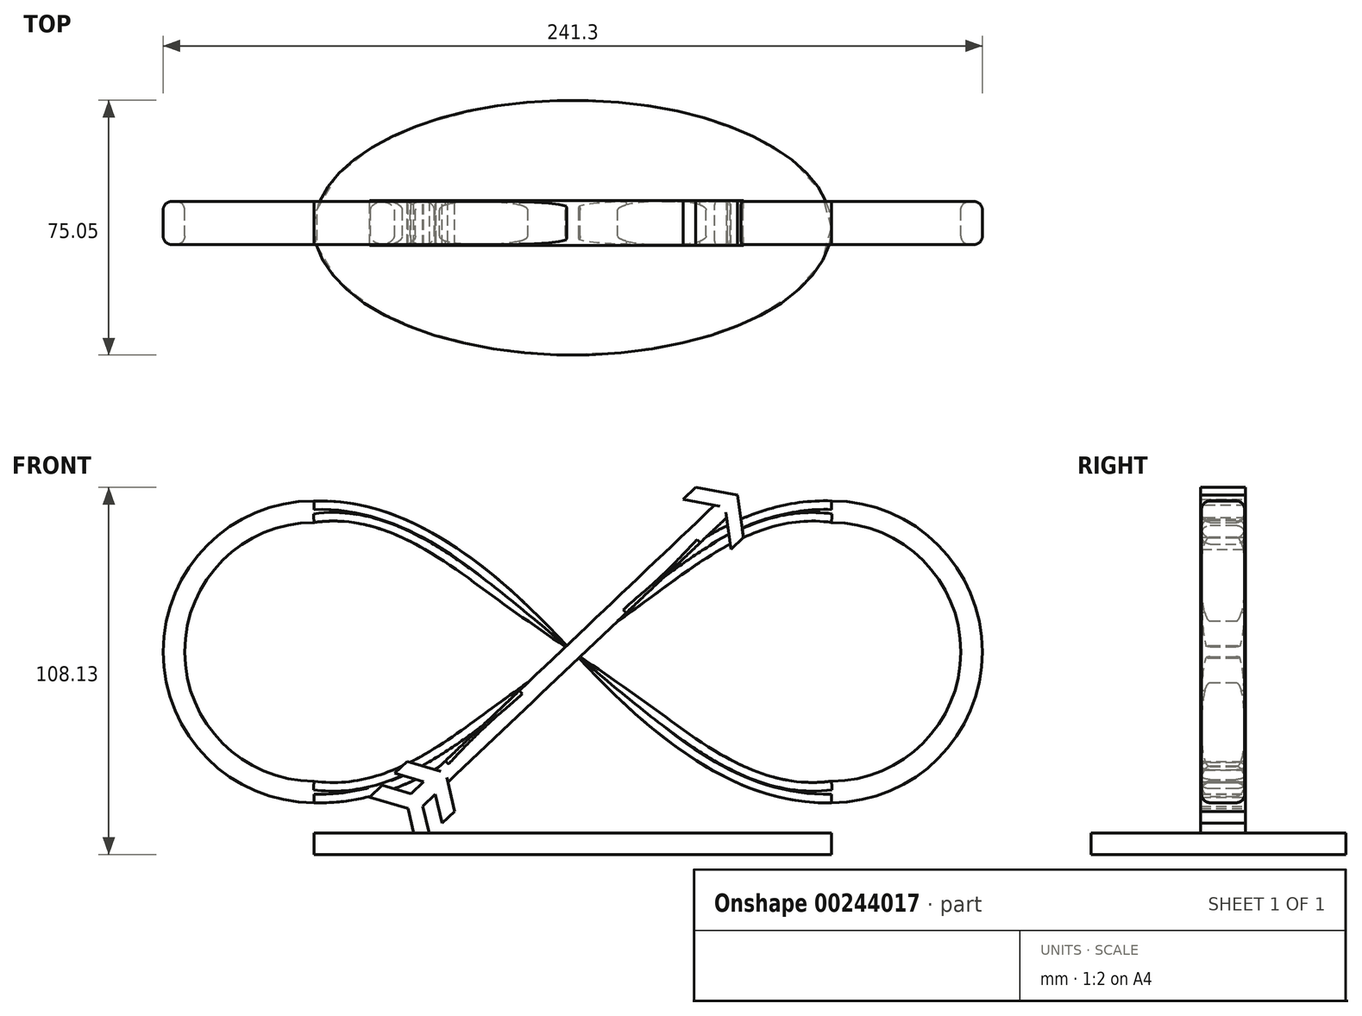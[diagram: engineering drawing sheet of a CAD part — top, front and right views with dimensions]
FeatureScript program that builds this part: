
annotation { "Feature Type Name" : "Feature", "Feature Type Description" : "" }
export const myFeature = defineFeature(function(context is Context, id is Id, definition is map)
    precondition{}
    {
        {
            var Q0;
            Q0=qCreatedBy(makeId("Front.planeOp"),FACE);
            var sketch = newSketch(context, id + "F0", { "sketchPlane" : qUnion([Q0])});
            skCircle(sketch, "E0", {"center": v(-76.2, 0) * mm, "radius": 38.1 * mm});
            skCircle(sketch, "E1", {"center": v(76.2, 0) * mm, "radius": 38.1 * mm});
            skFitSpline(sketch, "E2", {"points": [v(-76.2, 38.1) * mm, v(-25.4, 17.78) * mm, v(0, 0) * mm, v(25.4, -17.78) * mm, v(76.2, -38.1) * mm], "startDerivative": vector(211.41, 31.16) * mm, "endDerivative": vector(213.7, 30.04) * mm});
            skFitSpline(sketch, "E3", {"points": [v(76.2, 38.1) * mm, v(25.4, 17.78) * mm, v(0, 0) * mm, v(-25.4, -17.78) * mm, v(-76.2, -38.1) * mm], "startDerivative": vector(-211.41, 31.16) * mm, "endDerivative": vector(-211.41, 31.16) * mm});
            skCircle(sketch, "E4", {"center": v(-76.2, 0) * mm, "radius": 44.45 * mm});
            skCircle(sketch, "E5", {"center": v(76.2, 0) * mm, "radius": 44.45 * mm});
            skFitSpline(sketch, "E6", {"points": [v(-76.2, -44.45) * mm, v(-25.4, -24.13) * mm, v(0, 0) * mm, v(25.4, 24.13) * mm, v(76.2, 44.45) * mm], "startDerivative": vector(219.34, -7.84) * mm, "endDerivative": vector(219.34, -7.84) * mm});
            skFitSpline(sketch, "E7", {"points": [v(-76.2, 44.45) * mm, v(-25.4, 24.13) * mm, v(0, 0) * mm, v(25.4, -24.13) * mm, v(76.2, -44.45) * mm], "startDerivative": vector(219.34, 7.84) * mm, "endDerivative": vector(219.34, 7.84) * mm});
            skLineSegment(sketch, "E8", {"start": v(-48.54, -46.12) * mm, "end": v(48.54, 46.12) * mm});
            skLineSegment(sketch, "E9", {"start": v(-50.3, -44.27) * mm, "end": v(-48.54, -46.12) * mm});
            skLineSegment(sketch, "E10", {"start": v(-48.54, -46.12) * mm, "end": v(-46.8, -47.96) * mm});
            skLineSegment(sketch, "E11", {"start": v(-46.8, -47.96) * mm, "end": v(45.28, 39.51) * mm});
            skLineSegment(sketch, "E12", {"start": v(-48.54, -46.12) * mm, "end": v(-59.8, -42.79) * mm});
            skLineSegment(sketch, "E13", {"start": v(-59.8, -42.79) * mm, "end": v(-56.11, -39.3) * mm});
            skLineSegment(sketch, "E14", {"start": v(-56.11, -39.3) * mm, "end": v(-44.86, -42.62) * mm});
            skLineSegment(sketch, "E15", {"start": v(-44.86, -42.62) * mm, "end": v(-42.11, -54.02) * mm});
            skLineSegment(sketch, "E16", {"start": v(-42.11, -54.02) * mm, "end": v(-45.8, -57.52) * mm});
            skLineSegment(sketch, "E17", {"start": v(-45.8, -57.52) * mm, "end": v(-48.54, -46.12) * mm});
            skLineSegment(sketch, "E18", {"start": v(-41.18, -39.12) * mm, "end": v(-38.43, -50.52) * mm});
            skLineSegment(sketch, "E19", {"start": v(-38.43, -50.52) * mm, "end": v(-34.75, -47.03) * mm});
            skLineSegment(sketch, "E20", {"start": v(-34.75, -47.03) * mm, "end": v(-37.5, -35.62) * mm});
            skLineSegment(sketch, "E21", {"start": v(-37.5, -35.62) * mm, "end": v(-48.74, -32.3) * mm});
            skLineSegment(sketch, "E22", {"start": v(-48.74, -32.3) * mm, "end": v(-52.43, -35.8) * mm});
            skLineSegment(sketch, "E23", {"start": v(-52.43, -35.8) * mm, "end": v(-41.18, -39.12) * mm});
            skLineSegment(sketch, "E24", {"start": v(41.78, 43.2) * mm, "end": v(-50.3, -44.27) * mm});
            skLineSegment(sketch, "E25", {"start": v(41.78, 43.2) * mm, "end": v(32.55, 44.94) * mm});
            skLineSegment(sketch, "E26", {"start": v(32.55, 44.94) * mm, "end": v(36.23, 48.44) * mm});
            skLineSegment(sketch, "E27", {"start": v(36.23, 48.44) * mm, "end": v(48.54, 46.12) * mm});
            skLineSegment(sketch, "E28", {"start": v(45.28, 39.51) * mm, "end": v(46.55, 30.2) * mm});
            skLineSegment(sketch, "E29", {"start": v(46.55, 30.2) * mm, "end": v(50.23, 33.7) * mm});
            skLineSegment(sketch, "E30", {"start": v(50.23, 33.7) * mm, "end": v(48.54, 46.12) * mm});
            skSolve(sketch);
        }
        {
            var Q0;
            {var subQ0=sQuery(id+"F0.wireOp",EDGE,"E4");var subQ3=sQuery(id+"F0.wireOp",EDGE,"E7");var subQ5=makeQuery(id+"F0.imprint","INTERSECT",VERTEX,{"derivedFrom":[subQ0,subQ3]});Q0=makeQuery(id+"F0.imprint","IMPRINT",FACE,{"disambiguationData":[TD([[makeQuery(id+"F0.imprint","IMPRINT",EDGE,{"disambiguationData":[TD([[subQ5,1.0]])],"derivedFrom":subQ0}),-1.0]])]});}
            var Q1;
            {var subQ0=sQuery(id+"F0.wireOp",EDGE,"E4");var subQ3=sQuery(id+"F0.wireOp",EDGE,"E6");var subQ5=makeQuery(id+"F0.imprint","INTERSECT",VERTEX,{"derivedFrom":[subQ0,subQ3]});Q1=makeQuery(id+"F0.imprint","IMPRINT",FACE,{"disambiguationData":[TD([[makeQuery(id+"F0.imprint","IMPRINT",EDGE,{"disambiguationData":[TD([[subQ5,-1.0]])],"derivedFrom":subQ0}),-1.0]])]});}
            var Q2;
            {var subQ0=sQuery(id+"F0.wireOp",EDGE,"E5");var subQ3=sQuery(id+"F0.wireOp",EDGE,"E6");var subQ5=makeQuery(id+"F0.imprint","INTERSECT",VERTEX,{"derivedFrom":[subQ0,subQ3]});Q2=makeQuery(id+"F0.imprint","IMPRINT",FACE,{"disambiguationData":[TD([[makeQuery(id+"F0.imprint","IMPRINT",EDGE,{"disambiguationData":[TD([[subQ5,-1.0]])],"derivedFrom":subQ0}),-1.0]])]});}
            var Q3;
            {var subQ1=sQuery(id+"F0.wireOp",EDGE,"E1");var subQ5=sQuery(id+"F0.wireOp",EDGE,"E2");var subQ6=makeQuery(id+"F0.imprint","INTERSECT",VERTEX,{"derivedFrom":[subQ1,subQ5]});Q3=makeQuery(id+"F0.imprint","IMPRINT",FACE,{"disambiguationData":[TD([[makeQuery(id+"F0.imprint","IMPRINT",EDGE,{"disambiguationData":[TD([[subQ6,-1.0]])],"derivedFrom":subQ1}),-1.0]])]});}
            var Q4;
            {var subQ0=sQuery(id+"F0.wireOp",EDGE,"E13");var subQ1=sQuery(id+"F0.wireOp",EDGE,"E4");var subQ2=makeQuery(id+"F0.imprint","INTERSECT",VERTEX,{"derivedFrom":[subQ1,subQ0]});Q4=makeQuery(id+"F0.imprint","IMPRINT",FACE,{"disambiguationData":[TD([[makeQuery(id+"F0.imprint","IMPRINT",EDGE,{"disambiguationData":[TD([[subQ2,-1.0]])],"derivedFrom":subQ1}),-1.0]])]});}
            var Q5;
            {var subQ0=sQuery(id+"F0.wireOp",EDGE,"E13");var subQ1=sQuery(id+"F0.wireOp",EDGE,"E4");var subQ2=makeQuery(id+"F0.imprint","INTERSECT",VERTEX,{"derivedFrom":[subQ1,subQ0]});Q5=makeQuery(id+"F0.imprint","IMPRINT",FACE,{"disambiguationData":[TD([[makeQuery(id+"F0.imprint","IMPRINT",EDGE,{"disambiguationData":[TD([[subQ2,-1.0]])],"derivedFrom":subQ1}),1.0]])]});}
            var Q6;
            {var subQ14=sQuery(id+"F0.wireOp",EDGE,"E2");var subQ15=sQuery(id+"F0.wireOp",EDGE,"E0");var subQ16=makeQuery(id+"F0.imprint","INTERSECT",VERTEX,{"derivedFrom":[subQ15,subQ14]});Q6=makeQuery(id+"F0.imprint","IMPRINT",FACE,{"disambiguationData":[TD([[makeQuery(id+"F0.imprint","IMPRINT",EDGE,{"disambiguationData":[TD([[subQ16,-1.0]])],"derivedFrom":subQ15}),-1.0]])]});}
            var Q7;
            {var subQ3=sQuery(id+"F0.wireOp",EDGE,"E3");var subQ5=sQuery(id+"F0.wireOp",EDGE,"E21");var subQ6=makeQuery(id+"F0.imprint","INTERSECT",VERTEX,{"derivedFrom":[subQ3,subQ5]});Q7=makeQuery(id+"F0.imprint","IMPRINT",FACE,{"disambiguationData":[TD([[makeQuery(id+"F0.imprint","IMPRINT",EDGE,{"disambiguationData":[TD([[subQ6,-1.0]])],"derivedFrom":subQ3}),1.0]])]});}
            var Q8;
            {var subQ0=sQuery(id+"F0.wireOp",EDGE,"E14");var subQ1=sQuery(id+"F0.wireOp",EDGE,"E4");var subQ2=makeQuery(id+"F0.imprint","INTERSECT",VERTEX,{"derivedFrom":[subQ1,subQ0]});Q8=makeQuery(id+"F0.imprint","IMPRINT",FACE,{"disambiguationData":[TD([[makeQuery(id+"F0.imprint","IMPRINT",EDGE,{"disambiguationData":[TD([[subQ2,-1.0]])],"derivedFrom":subQ1}),-1.0]])]});}
            var Q9;
            {var subQ0=sQuery(id+"F0.wireOp",EDGE,"E23");var subQ1=sQuery(id+"F0.wireOp",EDGE,"E4");var subQ2=makeQuery(id+"F0.imprint","INTERSECT",VERTEX,{"derivedFrom":[subQ1,subQ0]});Q9=makeQuery(id+"F0.imprint","IMPRINT",FACE,{"disambiguationData":[TD([[makeQuery(id+"F0.imprint","IMPRINT",EDGE,{"disambiguationData":[TD([[subQ2,-1.0]])],"derivedFrom":subQ1}),-1.0]])]});}
            var Q10;
            {var subQ0=sQuery(id+"F0.wireOp",EDGE,"E4");var subQ1=sQuery(id+"F0.wireOp",EDGE,"E3");var subQ2=makeQuery(id+"F0.imprint","INTERSECT",VERTEX,{"derivedFrom":[subQ1,subQ0]});Q10=makeQuery(id+"F0.imprint","IMPRINT",FACE,{"disambiguationData":[TD([[makeQuery(id+"F0.imprint","IMPRINT",EDGE,{"disambiguationData":[TD([[subQ2,-1.0]])],"derivedFrom":subQ1}),1.0]])]});}
            var Q11;
            {var subQ1=sQuery(id+"F0.wireOp",EDGE,"E3");var subQ7=sQuery(id+"F0.wireOp",EDGE,"E24");var subQ9=makeQuery(id+"F0.imprint","INTERSECT",VERTEX,{"derivedFrom":[subQ1,subQ7]});Q11=makeQuery(id+"F0.imprint","IMPRINT",FACE,{"disambiguationData":[TD([[makeQuery(id+"F0.imprint","IMPRINT",EDGE,{"disambiguationData":[TD([[subQ9,-1.0]])],"derivedFrom":subQ1}),1.0]])]});}
            var Q12;
            {var subQ0=sQuery(id+"F0.wireOp",EDGE,"E24");var subQ4=sQuery(id+"F0.wireOp",EDGE,"E6");var subQ6=makeQuery(id+"F0.imprint","INTERSECT",VERTEX,{"derivedFrom":[subQ4,subQ0]});Q12=makeQuery(id+"F0.imprint","IMPRINT",FACE,{"disambiguationData":[TD([[makeQuery(id+"F0.imprint","IMPRINT",EDGE,{"disambiguationData":[TD([[subQ6,-1.0]])],"derivedFrom":subQ4}),1.0]])]});}
            var Q13;
            {var subQ0=sQuery(id+"F0.wireOp",EDGE,"E24");var subQ1=sQuery(id+"F0.wireOp",EDGE,"E2");var subQ2=makeQuery(id+"F0.imprint","INTERSECT",VERTEX,{"derivedFrom":[subQ1,subQ0]});Q13=makeQuery(id+"F0.imprint","IMPRINT",FACE,{"disambiguationData":[TD([[makeQuery(id+"F0.imprint","IMPRINT",EDGE,{"disambiguationData":[TD([[subQ2,-1.0]])],"derivedFrom":subQ0}),1.0]])]});}
            var Q14;
            {var subQ0=sQuery(id+"F0.wireOp",EDGE,"E11");var subQ3=sQuery(id+"F0.wireOp",EDGE,"E7");var subQ5=makeQuery(id+"F0.imprint","INTERSECT",VERTEX,{"derivedFrom":[subQ3,subQ0]});Q14=makeQuery(id+"F0.imprint","IMPRINT",FACE,{"disambiguationData":[TD([[makeQuery(id+"F0.imprint","IMPRINT",EDGE,{"disambiguationData":[TD([[subQ5,-1.0]])],"derivedFrom":subQ0}),1.0]])]});}
            var Q15;
            {var subQ0=sQuery(id+"F0.wireOp",EDGE,"E24");var subQ3=sQuery(id+"F0.wireOp",EDGE,"E7");var subQ5=makeQuery(id+"F0.imprint","INTERSECT",VERTEX,{"derivedFrom":[subQ3,subQ0]});Q15=makeQuery(id+"F0.imprint","IMPRINT",FACE,{"disambiguationData":[TD([[makeQuery(id+"F0.imprint","IMPRINT",EDGE,{"disambiguationData":[TD([[subQ5,-1.0]])],"derivedFrom":subQ0}),1.0]])]});}
            var Q16;
            {var subQ0=sQuery(id+"F0.wireOp",EDGE,"E8");var subQ1=sQuery(id+"F0.wireOp",EDGE,"E6");var subQ2=makeQuery(id+"F0.imprint","INTERSECT",VERTEX,{"disambiguationData":[OD(0.0)],"derivedFrom":[subQ1,subQ0]});Q16=makeQuery(id+"F0.imprint","IMPRINT",FACE,{"disambiguationData":[TD([[makeQuery(id+"F0.imprint","IMPRINT",EDGE,{"disambiguationData":[TD([[subQ2,-1.0]])],"derivedFrom":subQ1}),1.0]])]});}
            var Q17;
            {var subQ3=sQuery(id+"F0.wireOp",EDGE,"E8");var subQ4=sQuery(id+"F0.wireOp",EDGE,"E6");var subQ6=makeQuery(id+"F0.imprint","INTERSECT",VERTEX,{"disambiguationData":[OD(1.0)],"derivedFrom":[subQ4,subQ3]});Q17=makeQuery(id+"F0.imprint","IMPRINT",FACE,{"disambiguationData":[TD([[makeQuery(id+"F0.imprint","IMPRINT",EDGE,{"disambiguationData":[TD([[subQ6,-1.0]])],"derivedFrom":subQ4}),-1.0]])]});}
            var Q18;
            {var subQ0=sQuery(id+"F0.wireOp",EDGE,"E30");var subQ1=sQuery(id+"F0.wireOp",EDGE,"E5");var subQ2=makeQuery(id+"F0.imprint","INTERSECT",VERTEX,{"derivedFrom":[subQ1,subQ0]});Q18=makeQuery(id+"F0.imprint","IMPRINT",FACE,{"disambiguationData":[TD([[makeQuery(id+"F0.imprint","IMPRINT",EDGE,{"disambiguationData":[TD([[subQ2,-1.0]])],"derivedFrom":subQ1}),-1.0]])]});}
            var Q19;
            {var subQ1=sQuery(id+"F0.wireOp",EDGE,"E3");var subQ7=sQuery(id+"F0.wireOp",EDGE,"E29");var subQ9=makeQuery(id+"F0.imprint","INTERSECT",VERTEX,{"derivedFrom":[subQ1,subQ7]});Q19=makeQuery(id+"F0.imprint","IMPRINT",FACE,{"disambiguationData":[TD([[makeQuery(id+"F0.imprint","IMPRINT",EDGE,{"disambiguationData":[TD([[subQ9,-1.0]])],"derivedFrom":subQ1}),-1.0]])]});}
            var Q20;
            {var subQ1=sQuery(id+"F0.wireOp",EDGE,"E3");var subQ7=sQuery(id+"F0.wireOp",EDGE,"E5");var subQ8=makeQuery(id+"F0.imprint","INTERSECT",VERTEX,{"derivedFrom":[subQ1,subQ7]});Q20=makeQuery(id+"F0.imprint","IMPRINT",FACE,{"disambiguationData":[TD([[makeQuery(id+"F0.imprint","IMPRINT",EDGE,{"disambiguationData":[TD([[subQ8,-1.0]])],"derivedFrom":subQ1}),-1.0]])]});}
            var Q21;
            {var subQ0=sQuery(id+"F0.wireOp",EDGE,"E11");var subQ1=sQuery(id+"F0.wireOp",EDGE,"E2");var subQ2=makeQuery(id+"F0.imprint","INTERSECT",VERTEX,{"derivedFrom":[subQ1,subQ0]});Q21=makeQuery(id+"F0.imprint","IMPRINT",FACE,{"disambiguationData":[TD([[makeQuery(id+"F0.imprint","IMPRINT",EDGE,{"disambiguationData":[TD([[subQ2,-1.0]])],"derivedFrom":subQ1}),-1.0]])]});}
            var Q22;
            {var subQ0=sQuery(id+"F0.wireOp",EDGE,"E28");var subQ1=sQuery(id+"F0.wireOp",EDGE,"E3");var subQ2=makeQuery(id+"F0.imprint","INTERSECT",VERTEX,{"derivedFrom":[subQ1,subQ0]});Q22=makeQuery(id+"F0.imprint","IMPRINT",FACE,{"disambiguationData":[TD([[makeQuery(id+"F0.imprint","IMPRINT",EDGE,{"disambiguationData":[TD([[subQ2,-1.0]])],"derivedFrom":subQ1}),-1.0]])]});}
            var Q23;
            {var subQ0=sQuery(id+"F0.wireOp",EDGE,"E8");var subQ1=sQuery(id+"F0.wireOp",EDGE,"E6");var subQ2=makeQuery(id+"F0.imprint","INTERSECT",VERTEX,{"disambiguationData":[OD(1.0)],"derivedFrom":[subQ1,subQ0]});Q23=makeQuery(id+"F0.imprint","IMPRINT",FACE,{"disambiguationData":[TD([[makeQuery(id+"F0.imprint","IMPRINT",EDGE,{"disambiguationData":[TD([[subQ2,1.0]])],"derivedFrom":subQ1}),-1.0]])]});}
            var Q24;
            {var subQ0=sQuery(id+"F0.wireOp",EDGE,"E11");var subQ1=sQuery(id+"F0.wireOp",EDGE,"E2");var subQ2=makeQuery(id+"F0.imprint","INTERSECT",VERTEX,{"derivedFrom":[subQ1,subQ0]});Q24=makeQuery(id+"F0.imprint","IMPRINT",FACE,{"disambiguationData":[TD([[makeQuery(id+"F0.imprint","IMPRINT",EDGE,{"disambiguationData":[TD([[subQ2,-1.0]])],"derivedFrom":subQ0}),1.0]])]});}
            extrude(context, id + "F1", {"entities" : qUnion([Q0, Q1, Q2, Q3, Q4, Q5, Q6, Q7, Q8, Q9, Q10, Q11, Q12, Q13, Q14, Q15, Q16, Q17, Q18, Q19, Q20, Q21, Q22, Q23, Q24]), "depth" : 6.35 * mm, "hasSecondDirection" : true, "secondDirectionOppositeDirection" : true, "secondDirectionDepth" : 6.35 * mm});
        }
        {
            var Q0;
            {var subQ0=sQuery(id+"F0.wireOp",EDGE,"E2");var subQ1=makeQuery(id+"F0.imprint","INTERSECT",VERTEX,{"derivedFrom":[subQ0,sQuery(id+"F0.wireOp",EDGE,"E4")]});Q0=makeQuery(id+"F1.opExtrude","CAP_EDGE",EDGE,{"disambiguationData":[OSD([subQ0]),TDD([makeQuery(id+"F0.imprint","IMPRINT",EDGE,{"disambiguationData":[TD([[makeQuery(id+"F0.imprint","INTERSECT",VERTEX,{"derivedFrom":[sQuery(id+"F0.wireOp",EDGE,"E0"),subQ0]}),-1.0]])],"derivedFrom":subQ0}),makeQuery(id+"F0.imprint","IMPRINT",EDGE,{"disambiguationData":[TD([[subQ1,-1.0]])],"derivedFrom":subQ0})])],"isStart":true});}
            var Q1;
            {var subQ0=sQuery(id+"F0.wireOp",EDGE,"E7");var subQ1=makeQuery(id+"F0.imprint","INTERSECT",VERTEX,{"derivedFrom":[subQ0,sQuery(id+"F0.wireOp",EDGE,"E24")]});Q1=makeQuery(id+"F1.opExtrude","CAP_EDGE",EDGE,{"disambiguationData":[OSD([subQ0]),TDD([makeQuery(id+"F0.imprint","IMPRINT",EDGE,{"disambiguationData":[TD([[makeQuery(id+"F0.imprint","INTERSECT",VERTEX,{"derivedFrom":[sQuery(id+"F0.wireOp",EDGE,"E4"),subQ0]}),-1.0]])],"derivedFrom":subQ0}),makeQuery(id+"F0.imprint","IMPRINT",EDGE,{"disambiguationData":[TD([[subQ1,-1.0]])],"derivedFrom":subQ0})])],"isStart":true});}
            var Q2;
            Q2=makeQuery(id+"F1.opExtrude","CAP_EDGE",EDGE,{"disambiguationData":[OSD([sQuery(id+"F0.wireOp",EDGE,"E24")])],"isStart":true});
            var Q3;
            {var subQ0=sQuery(id+"F0.wireOp",EDGE,"E8");var subQ1=sQuery(id+"F0.wireOp",EDGE,"E6");var subQ2=makeQuery(id+"F0.imprint","INTERSECT",VERTEX,{"disambiguationData":[OD(0.0)],"derivedFrom":[subQ1,subQ0]});var subQ3=makeQuery(id+"F0.imprint","INTERSECT",VERTEX,{"derivedFrom":[subQ1,sQuery(id+"F0.wireOp",EDGE,"E24")]});var subQ4=makeQuery(id+"F0.imprint","INTERSECT",VERTEX,{"derivedFrom":[subQ1,sQuery(id+"F0.wireOp",EDGE,"E21")]});var subQ5=makeQuery(id+"F0.imprint","INTERSECT",VERTEX,{"derivedFrom":[subQ1,sQuery(id+"F0.wireOp",EDGE,"E23")]});var subQ6=makeQuery(id+"F0.imprint","INTERSECT",VERTEX,{"derivedFrom":[subQ1,sQuery(id+"F0.wireOp",EDGE,"E14")]});var subQ7=makeQuery(id+"F0.imprint","INTERSECT",VERTEX,{"derivedFrom":[subQ1,sQuery(id+"F0.wireOp",EDGE,"E13")]});Q3=makeQuery(id+"F1.opExtrude","CAP_EDGE",EDGE,{"disambiguationData":[OSD([subQ1]),TDD([makeQuery(id+"F0.imprint","IMPRINT",EDGE,{"disambiguationData":[TD([[makeQuery(id+"F0.imprint","INTERSECT",VERTEX,{"derivedFrom":[sQuery(id+"F0.wireOp",EDGE,"E4"),subQ1]}),-1.0]])],"derivedFrom":subQ1}),makeQuery(id+"F0.imprint","IMPRINT",EDGE,{"disambiguationData":[TD([[subQ7,-1.0]])],"derivedFrom":subQ1}),makeQuery(id+"F0.imprint","IMPRINT",EDGE,{"disambiguationData":[TD([[subQ6,-1.0]])],"derivedFrom":subQ1}),makeQuery(id+"F0.imprint","IMPRINT",EDGE,{"disambiguationData":[TD([[subQ5,-1.0]])],"derivedFrom":subQ1}),makeQuery(id+"F0.imprint","IMPRINT",EDGE,{"disambiguationData":[TD([[subQ4,-1.0]])],"derivedFrom":subQ1}),makeQuery(id+"F0.imprint","IMPRINT",EDGE,{"disambiguationData":[TD([[subQ3,-1.0]])],"derivedFrom":subQ1}),makeQuery(id+"F0.imprint","IMPRINT",EDGE,{"disambiguationData":[TD([[subQ2,-1.0]])],"derivedFrom":subQ1})])],"isStart":true});}
            var Q4;
            {var subQ0=sQuery(id+"F0.wireOp",EDGE,"E6");var subQ1=makeQuery(id+"F0.imprint","INTERSECT",VERTEX,{"derivedFrom":[subQ0,sQuery(id+"F0.wireOp",EDGE,"E30")]});var subQ3=makeQuery(id+"F0.imprint","INTERSECT",VERTEX,{"derivedFrom":[subQ0,sQuery(id+"F0.wireOp",EDGE,"E11")]});var subQ4=sQuery(id+"F0.wireOp",EDGE,"E8");var subQ5=makeQuery(id+"F0.imprint","INTERSECT",VERTEX,{"disambiguationData":[OD(1.0)],"derivedFrom":[subQ0,subQ4]});Q4=makeQuery(id+"F1.opExtrude","CAP_EDGE",EDGE,{"disambiguationData":[OSD([subQ0]),TDD([makeQuery(id+"F0.imprint","IMPRINT",EDGE,{"disambiguationData":[TD([[subQ5,1.0]])],"derivedFrom":subQ0}),makeQuery(id+"F0.imprint","IMPRINT",EDGE,{"disambiguationData":[TD([[subQ5,-1.0]])],"derivedFrom":subQ0}),makeQuery(id+"F0.imprint","IMPRINT",EDGE,{"disambiguationData":[TD([[subQ3,-1.0]])],"derivedFrom":subQ0}),makeQuery(id+"F0.imprint","IMPRINT",EDGE,{"disambiguationData":[TD([[subQ1,1.0]])],"derivedFrom":subQ0}),makeQuery(id+"F0.imprint","IMPRINT",EDGE,{"disambiguationData":[TD([[makeQuery(id+"F0.imprint","INTERSECT",VERTEX,{"derivedFrom":[sQuery(id+"F0.wireOp",EDGE,"E5"),subQ0]}),1.0]])],"derivedFrom":subQ0})])],"isStart":true});}
            var Q5;
            {var subQ0=sQuery(id+"F0.wireOp",EDGE,"E2");Q5=makeQuery(id+"F1.opExtrude","CAP_EDGE",EDGE,{"disambiguationData":[OSD([subQ0]),TDD([makeQuery(id+"F0.imprint","IMPRINT",EDGE,{"disambiguationData":[TD([[makeQuery(id+"F0.imprint","INTERSECT",VERTEX,{"derivedFrom":[subQ0,sQuery(id+"F0.wireOp",EDGE,"E11")]}),-1.0]])],"derivedFrom":subQ0}),makeQuery(id+"F0.imprint","IMPRINT",EDGE,{"disambiguationData":[TD([[makeQuery(id+"F0.imprint","INTERSECT",VERTEX,{"derivedFrom":[sQuery(id+"F0.wireOp",EDGE,"E1"),subQ0]}),1.0]])],"derivedFrom":subQ0})])],"isStart":true});}
            var Q6;
            {var subQ0=sQuery(id+"F0.wireOp",EDGE,"E7");var subQ1=makeQuery(id+"F0.imprint","INTERSECT",VERTEX,{"derivedFrom":[subQ0,sQuery(id+"F0.wireOp",EDGE,"E11")]});Q6=makeQuery(id+"F1.opExtrude","CAP_EDGE",EDGE,{"disambiguationData":[OSD([subQ0]),TDD([makeQuery(id+"F0.imprint","IMPRINT",EDGE,{"disambiguationData":[TD([[subQ1,1.0]])],"derivedFrom":subQ0}),makeQuery(id+"F0.imprint","IMPRINT",EDGE,{"disambiguationData":[TD([[makeQuery(id+"F0.imprint","INTERSECT",VERTEX,{"derivedFrom":[sQuery(id+"F0.wireOp",EDGE,"E5"),subQ0]}),1.0]])],"derivedFrom":subQ0})])],"isStart":true});}
            var Q7;
            {var subQ0=sQuery(id+"F0.wireOp",EDGE,"E3");var subQ2=makeQuery(id+"F0.imprint","INTERSECT",VERTEX,{"derivedFrom":[subQ0,sQuery(id+"F0.wireOp",EDGE,"E21")]});var subQ3=makeQuery(id+"F0.imprint","INTERSECT",VERTEX,{"derivedFrom":[subQ0,sQuery(id+"F0.wireOp",EDGE,"E4")]});Q7=makeQuery(id+"F1.opExtrude","CAP_EDGE",EDGE,{"disambiguationData":[OSD([subQ0]),TDD([makeQuery(id+"F0.imprint","IMPRINT",EDGE,{"disambiguationData":[TD([[makeQuery(id+"F0.imprint","INTERSECT",VERTEX,{"derivedFrom":[subQ0,sQuery(id+"F0.wireOp",EDGE,"E24")]}),-1.0]])],"derivedFrom":subQ0}),makeQuery(id+"F0.imprint","IMPRINT",EDGE,{"disambiguationData":[TD([[subQ3,-1.0]])],"derivedFrom":subQ0}),makeQuery(id+"F0.imprint","IMPRINT",EDGE,{"disambiguationData":[TD([[subQ2,-1.0]])],"derivedFrom":subQ0}),makeQuery(id+"F0.imprint","IMPRINT",EDGE,{"disambiguationData":[TD([[makeQuery(id+"F0.imprint","INTERSECT",VERTEX,{"derivedFrom":[sQuery(id+"F0.wireOp",EDGE,"E0"),subQ0]}),1.0]])],"derivedFrom":subQ0})])],"isStart":true});}
            var Q8;
            {var subQ0=sQuery(id+"F0.wireOp",EDGE,"E3");var subQ2=makeQuery(id+"F0.imprint","INTERSECT",VERTEX,{"derivedFrom":[subQ0,sQuery(id+"F0.wireOp",EDGE,"E21")]});var subQ3=makeQuery(id+"F0.imprint","INTERSECT",VERTEX,{"derivedFrom":[subQ0,sQuery(id+"F0.wireOp",EDGE,"E4")]});Q8=makeQuery(id+"F1.opExtrude","CAP_EDGE",EDGE,{"disambiguationData":[OSD([subQ0]),TDD([makeQuery(id+"F0.imprint","IMPRINT",EDGE,{"disambiguationData":[TD([[makeQuery(id+"F0.imprint","INTERSECT",VERTEX,{"derivedFrom":[subQ0,sQuery(id+"F0.wireOp",EDGE,"E24")]}),-1.0]])],"derivedFrom":subQ0}),makeQuery(id+"F0.imprint","IMPRINT",EDGE,{"disambiguationData":[TD([[subQ3,-1.0]])],"derivedFrom":subQ0}),makeQuery(id+"F0.imprint","IMPRINT",EDGE,{"disambiguationData":[TD([[subQ2,-1.0]])],"derivedFrom":subQ0}),makeQuery(id+"F0.imprint","IMPRINT",EDGE,{"disambiguationData":[TD([[makeQuery(id+"F0.imprint","INTERSECT",VERTEX,{"derivedFrom":[sQuery(id+"F0.wireOp",EDGE,"E0"),subQ0]}),1.0]])],"derivedFrom":subQ0})])],"isStart":false});}
            var Q9;
            Q9=makeQuery(id+"F1.opExtrude","CAP_EDGE",EDGE,{"disambiguationData":[OSD([sQuery(id+"F0.wireOp",EDGE,"E4")])],"isStart":true});
            var Q10;
            Q10=makeQuery(id+"F1.opExtrude","CAP_EDGE",EDGE,{"disambiguationData":[OSD([sQuery(id+"F0.wireOp",EDGE,"E0")])],"isStart":false});
            var Q11;
            Q11=makeQuery(id+"F1.opExtrude","CAP_EDGE",EDGE,{"disambiguationData":[OSD([sQuery(id+"F0.wireOp",EDGE,"E4")])],"isStart":false});
            var Q12;
            {var subQ0=sQuery(id+"F0.wireOp",EDGE,"E7");var subQ1=makeQuery(id+"F0.imprint","INTERSECT",VERTEX,{"derivedFrom":[subQ0,sQuery(id+"F0.wireOp",EDGE,"E24")]});Q12=makeQuery(id+"F1.opExtrude","CAP_EDGE",EDGE,{"disambiguationData":[OSD([subQ0]),TDD([makeQuery(id+"F0.imprint","IMPRINT",EDGE,{"disambiguationData":[TD([[makeQuery(id+"F0.imprint","INTERSECT",VERTEX,{"derivedFrom":[sQuery(id+"F0.wireOp",EDGE,"E4"),subQ0]}),-1.0]])],"derivedFrom":subQ0}),makeQuery(id+"F0.imprint","IMPRINT",EDGE,{"disambiguationData":[TD([[subQ1,-1.0]])],"derivedFrom":subQ0})])],"isStart":false});}
            var Q13;
            {var subQ0=sQuery(id+"F0.wireOp",EDGE,"E2");var subQ1=makeQuery(id+"F0.imprint","INTERSECT",VERTEX,{"derivedFrom":[subQ0,sQuery(id+"F0.wireOp",EDGE,"E4")]});Q13=makeQuery(id+"F1.opExtrude","CAP_EDGE",EDGE,{"disambiguationData":[OSD([subQ0]),TDD([makeQuery(id+"F0.imprint","IMPRINT",EDGE,{"disambiguationData":[TD([[makeQuery(id+"F0.imprint","INTERSECT",VERTEX,{"derivedFrom":[sQuery(id+"F0.wireOp",EDGE,"E0"),subQ0]}),-1.0]])],"derivedFrom":subQ0}),makeQuery(id+"F0.imprint","IMPRINT",EDGE,{"disambiguationData":[TD([[subQ1,-1.0]])],"derivedFrom":subQ0})])],"isStart":false});}
            var Q14;
            Q14=makeQuery(id+"F1.opExtrude","CAP_EDGE",EDGE,{"disambiguationData":[OSD([sQuery(id+"F0.wireOp",EDGE,"E5")])],"isStart":false});
            var Q15;
            Q15=makeQuery(id+"F1.opExtrude","CAP_EDGE",EDGE,{"disambiguationData":[OSD([sQuery(id+"F0.wireOp",EDGE,"E5")])],"isStart":true});
            var Q16;
            Q16=makeQuery(id+"F1.opExtrude","CAP_EDGE",EDGE,{"disambiguationData":[OSD([sQuery(id+"F0.wireOp",EDGE,"E1")])],"isStart":false});
            var Q17;
            {var subQ0=sQuery(id+"F0.wireOp",EDGE,"E6");var subQ1=makeQuery(id+"F0.imprint","INTERSECT",VERTEX,{"derivedFrom":[subQ0,sQuery(id+"F0.wireOp",EDGE,"E30")]});var subQ3=makeQuery(id+"F0.imprint","INTERSECT",VERTEX,{"derivedFrom":[subQ0,sQuery(id+"F0.wireOp",EDGE,"E11")]});var subQ4=sQuery(id+"F0.wireOp",EDGE,"E8");var subQ5=makeQuery(id+"F0.imprint","INTERSECT",VERTEX,{"disambiguationData":[OD(1.0)],"derivedFrom":[subQ0,subQ4]});Q17=makeQuery(id+"F1.opExtrude","CAP_EDGE",EDGE,{"disambiguationData":[OSD([subQ0]),TDD([makeQuery(id+"F0.imprint","IMPRINT",EDGE,{"disambiguationData":[TD([[subQ5,1.0]])],"derivedFrom":subQ0}),makeQuery(id+"F0.imprint","IMPRINT",EDGE,{"disambiguationData":[TD([[subQ5,-1.0]])],"derivedFrom":subQ0}),makeQuery(id+"F0.imprint","IMPRINT",EDGE,{"disambiguationData":[TD([[subQ3,-1.0]])],"derivedFrom":subQ0}),makeQuery(id+"F0.imprint","IMPRINT",EDGE,{"disambiguationData":[TD([[subQ1,1.0]])],"derivedFrom":subQ0}),makeQuery(id+"F0.imprint","IMPRINT",EDGE,{"disambiguationData":[TD([[makeQuery(id+"F0.imprint","INTERSECT",VERTEX,{"derivedFrom":[sQuery(id+"F0.wireOp",EDGE,"E5"),subQ0]}),1.0]])],"derivedFrom":subQ0})])],"isStart":false});}
            var Q18;
            {var subQ0=sQuery(id+"F0.wireOp",EDGE,"E3");var subQ1=makeQuery(id+"F0.imprint","INTERSECT",VERTEX,{"derivedFrom":[subQ0,sQuery(id+"F0.wireOp",EDGE,"E5")]});var subQ2=makeQuery(id+"F0.imprint","INTERSECT",VERTEX,{"derivedFrom":[subQ0,sQuery(id+"F0.wireOp",EDGE,"E28")]});var subQ3=makeQuery(id+"F0.imprint","INTERSECT",VERTEX,{"derivedFrom":[subQ0,sQuery(id+"F0.wireOp",EDGE,"E29")]});Q18=makeQuery(id+"F1.opExtrude","CAP_EDGE",EDGE,{"disambiguationData":[OSD([subQ0]),TDD([makeQuery(id+"F0.imprint","IMPRINT",EDGE,{"disambiguationData":[TD([[makeQuery(id+"F0.imprint","INTERSECT",VERTEX,{"derivedFrom":[sQuery(id+"F0.wireOp",EDGE,"E1"),subQ0]}),-1.0]])],"derivedFrom":subQ0}),makeQuery(id+"F0.imprint","IMPRINT",EDGE,{"disambiguationData":[TD([[subQ3,-1.0]])],"derivedFrom":subQ0}),makeQuery(id+"F0.imprint","IMPRINT",EDGE,{"disambiguationData":[TD([[subQ2,-1.0]])],"derivedFrom":subQ0}),makeQuery(id+"F0.imprint","IMPRINT",EDGE,{"disambiguationData":[TD([[subQ1,-1.0]])],"derivedFrom":subQ0})])],"isStart":false});}
            var Q19;
            {var subQ0=sQuery(id+"F0.wireOp",EDGE,"E2");Q19=makeQuery(id+"F1.opExtrude","CAP_EDGE",EDGE,{"disambiguationData":[OSD([subQ0]),TDD([makeQuery(id+"F0.imprint","IMPRINT",EDGE,{"disambiguationData":[TD([[makeQuery(id+"F0.imprint","INTERSECT",VERTEX,{"derivedFrom":[subQ0,sQuery(id+"F0.wireOp",EDGE,"E11")]}),-1.0]])],"derivedFrom":subQ0}),makeQuery(id+"F0.imprint","IMPRINT",EDGE,{"disambiguationData":[TD([[makeQuery(id+"F0.imprint","INTERSECT",VERTEX,{"derivedFrom":[sQuery(id+"F0.wireOp",EDGE,"E1"),subQ0]}),1.0]])],"derivedFrom":subQ0})])],"isStart":false});}
            var Q20;
            {var subQ0=sQuery(id+"F0.wireOp",EDGE,"E7");var subQ1=makeQuery(id+"F0.imprint","INTERSECT",VERTEX,{"derivedFrom":[subQ0,sQuery(id+"F0.wireOp",EDGE,"E11")]});Q20=makeQuery(id+"F1.opExtrude","CAP_EDGE",EDGE,{"disambiguationData":[OSD([subQ0]),TDD([makeQuery(id+"F0.imprint","IMPRINT",EDGE,{"disambiguationData":[TD([[subQ1,1.0]])],"derivedFrom":subQ0}),makeQuery(id+"F0.imprint","IMPRINT",EDGE,{"disambiguationData":[TD([[makeQuery(id+"F0.imprint","INTERSECT",VERTEX,{"derivedFrom":[sQuery(id+"F0.wireOp",EDGE,"E5"),subQ0]}),1.0]])],"derivedFrom":subQ0})])],"isStart":false});}
            var Q21;
            {var subQ0=sQuery(id+"F0.wireOp",EDGE,"E8");var subQ1=sQuery(id+"F0.wireOp",EDGE,"E6");var subQ2=makeQuery(id+"F0.imprint","INTERSECT",VERTEX,{"disambiguationData":[OD(0.0)],"derivedFrom":[subQ1,subQ0]});var subQ3=makeQuery(id+"F0.imprint","INTERSECT",VERTEX,{"derivedFrom":[subQ1,sQuery(id+"F0.wireOp",EDGE,"E24")]});var subQ4=makeQuery(id+"F0.imprint","INTERSECT",VERTEX,{"derivedFrom":[subQ1,sQuery(id+"F0.wireOp",EDGE,"E21")]});var subQ5=makeQuery(id+"F0.imprint","INTERSECT",VERTEX,{"derivedFrom":[subQ1,sQuery(id+"F0.wireOp",EDGE,"E23")]});var subQ6=makeQuery(id+"F0.imprint","INTERSECT",VERTEX,{"derivedFrom":[subQ1,sQuery(id+"F0.wireOp",EDGE,"E14")]});var subQ7=makeQuery(id+"F0.imprint","INTERSECT",VERTEX,{"derivedFrom":[subQ1,sQuery(id+"F0.wireOp",EDGE,"E13")]});Q21=makeQuery(id+"F1.opExtrude","CAP_EDGE",EDGE,{"disambiguationData":[OSD([subQ1]),TDD([makeQuery(id+"F0.imprint","IMPRINT",EDGE,{"disambiguationData":[TD([[makeQuery(id+"F0.imprint","INTERSECT",VERTEX,{"derivedFrom":[sQuery(id+"F0.wireOp",EDGE,"E4"),subQ1]}),-1.0]])],"derivedFrom":subQ1}),makeQuery(id+"F0.imprint","IMPRINT",EDGE,{"disambiguationData":[TD([[subQ7,-1.0]])],"derivedFrom":subQ1}),makeQuery(id+"F0.imprint","IMPRINT",EDGE,{"disambiguationData":[TD([[subQ6,-1.0]])],"derivedFrom":subQ1}),makeQuery(id+"F0.imprint","IMPRINT",EDGE,{"disambiguationData":[TD([[subQ5,-1.0]])],"derivedFrom":subQ1}),makeQuery(id+"F0.imprint","IMPRINT",EDGE,{"disambiguationData":[TD([[subQ4,-1.0]])],"derivedFrom":subQ1}),makeQuery(id+"F0.imprint","IMPRINT",EDGE,{"disambiguationData":[TD([[subQ3,-1.0]])],"derivedFrom":subQ1}),makeQuery(id+"F0.imprint","IMPRINT",EDGE,{"disambiguationData":[TD([[subQ2,-1.0]])],"derivedFrom":subQ1})])],"isStart":false});}
            var Q22;
            Q22=makeQuery(id+"F1.opExtrude","CAP_EDGE",EDGE,{"disambiguationData":[OSD([sQuery(id+"F0.wireOp",EDGE,"E24")])],"isStart":false});
            var Q23;
            Q23=makeQuery(id+"F1.opExtrude","CAP_EDGE",EDGE,{"disambiguationData":[OSD([sQuery(id+"F0.wireOp",EDGE,"E1")])],"isStart":true});
            var Q24;
            {var subQ0=sQuery(id+"F0.wireOp",EDGE,"E3");var subQ1=makeQuery(id+"F0.imprint","INTERSECT",VERTEX,{"derivedFrom":[subQ0,sQuery(id+"F0.wireOp",EDGE,"E5")]});var subQ2=makeQuery(id+"F0.imprint","INTERSECT",VERTEX,{"derivedFrom":[subQ0,sQuery(id+"F0.wireOp",EDGE,"E28")]});var subQ3=makeQuery(id+"F0.imprint","INTERSECT",VERTEX,{"derivedFrom":[subQ0,sQuery(id+"F0.wireOp",EDGE,"E29")]});Q24=makeQuery(id+"F1.opExtrude","CAP_EDGE",EDGE,{"disambiguationData":[OSD([subQ0]),TDD([makeQuery(id+"F0.imprint","IMPRINT",EDGE,{"disambiguationData":[TD([[makeQuery(id+"F0.imprint","INTERSECT",VERTEX,{"derivedFrom":[sQuery(id+"F0.wireOp",EDGE,"E1"),subQ0]}),-1.0]])],"derivedFrom":subQ0}),makeQuery(id+"F0.imprint","IMPRINT",EDGE,{"disambiguationData":[TD([[subQ3,-1.0]])],"derivedFrom":subQ0}),makeQuery(id+"F0.imprint","IMPRINT",EDGE,{"disambiguationData":[TD([[subQ2,-1.0]])],"derivedFrom":subQ0}),makeQuery(id+"F0.imprint","IMPRINT",EDGE,{"disambiguationData":[TD([[subQ1,-1.0]])],"derivedFrom":subQ0})])],"isStart":true});}
            var Q25;
            Q25=makeQuery(id+"F1.opExtrude","CAP_EDGE",EDGE,{"disambiguationData":[OSD([sQuery(id+"F0.wireOp",EDGE,"E0")])],"isStart":true});
            var Q26;
            Q26=makeQuery(id+"F1.opExtrude","CAP_EDGE",EDGE,{"disambiguationData":[OSD([sQuery(id+"F0.wireOp",EDGE,"E11")])],"isStart":true});
            var Q27;
            Q27=makeQuery(id+"F1.opExtrude","CAP_EDGE",EDGE,{"disambiguationData":[OSD([sQuery(id+"F0.wireOp",EDGE,"E11")])],"isStart":false});
            fillet(context, id + "F2", {"entities" : qUnion([Q0, Q1, Q2, Q3, Q4, Q5, Q6, Q7, Q8, Q9, Q10, Q11, Q12, Q13, Q14, Q15, Q16, Q17, Q18, Q19, Q20, Q21, Q22, Q23, Q24, Q25, Q26, Q27]), "radius" : 2.54 * mm, "tangentPropagation" : true, "allowEdgeOverflow" : false});
        }
        {
            var Q0;
            {var subQ0=sQuery(id+"F0.wireOp",EDGE,"E24");var subQ1=sQuery(id+"F0.wireOp",EDGE,"E6");var subQ2=makeQuery(id+"F0.imprint","INTERSECT",VERTEX,{"derivedFrom":[subQ1,subQ0]});Q0=makeQuery(id+"F0.imprint","IMPRINT",FACE,{"disambiguationData":[TD([[makeQuery(id+"F0.imprint","IMPRINT",EDGE,{"disambiguationData":[TD([[subQ2,-1.0]])],"derivedFrom":subQ1}),-1.0]])]});}
            var Q1;
            {var subQ3=sQuery(id+"F0.wireOp",EDGE,"E21");var subQ5=sQuery(id+"F0.wireOp",EDGE,"E24");var subQ6=makeQuery(id+"F0.imprint","INTERSECT",VERTEX,{"derivedFrom":[subQ3,subQ5]});Q1=makeQuery(id+"F0.imprint","IMPRINT",FACE,{"disambiguationData":[TD([[makeQuery(id+"F0.imprint","IMPRINT",EDGE,{"disambiguationData":[TD([[subQ6,-1.0]])],"derivedFrom":subQ5}),1.0]])]});}
            var Q2;
            {var subQ0=sQuery(id+"F0.wireOp",EDGE,"E23");var subQ1=sQuery(id+"F0.wireOp",EDGE,"E6");var subQ2=makeQuery(id+"F0.imprint","INTERSECT",VERTEX,{"derivedFrom":[subQ1,subQ0]});Q2=makeQuery(id+"F0.imprint","IMPRINT",FACE,{"disambiguationData":[TD([[makeQuery(id+"F0.imprint","IMPRINT",EDGE,{"disambiguationData":[TD([[subQ2,-1.0]])],"derivedFrom":subQ1}),-1.0]])]});}
            var Q3;
            {var subQ0=sQuery(id+"F0.wireOp",EDGE,"E23");var subQ1=sQuery(id+"F0.wireOp",EDGE,"E4");var subQ2=makeQuery(id+"F0.imprint","INTERSECT",VERTEX,{"derivedFrom":[subQ1,subQ0]});Q3=makeQuery(id+"F0.imprint","IMPRINT",FACE,{"disambiguationData":[TD([[makeQuery(id+"F0.imprint","IMPRINT",EDGE,{"disambiguationData":[TD([[subQ2,-1.0]])],"derivedFrom":subQ1}),-1.0]])]});}
            var Q4;
            {var subQ3=sQuery(id+"F0.wireOp",EDGE,"E3");var subQ5=sQuery(id+"F0.wireOp",EDGE,"E21");var subQ6=makeQuery(id+"F0.imprint","INTERSECT",VERTEX,{"derivedFrom":[subQ3,subQ5]});Q4=makeQuery(id+"F0.imprint","IMPRINT",FACE,{"disambiguationData":[TD([[makeQuery(id+"F0.imprint","IMPRINT",EDGE,{"disambiguationData":[TD([[subQ6,-1.0]])],"derivedFrom":subQ3}),1.0]])]});}
            var Q5;
            {var subQ0=sQuery(id+"F0.wireOp",EDGE,"E21");var subQ1=sQuery(id+"F0.wireOp",EDGE,"E3");var subQ2=makeQuery(id+"F0.imprint","INTERSECT",VERTEX,{"derivedFrom":[subQ1,subQ0]});Q5=makeQuery(id+"F0.imprint","IMPRINT",FACE,{"disambiguationData":[TD([[makeQuery(id+"F0.imprint","IMPRINT",EDGE,{"disambiguationData":[TD([[subQ2,-1.0]])],"derivedFrom":subQ1}),-1.0]])]});}
            var Q6;
            {var subQ0=sQuery(id+"F0.wireOp",EDGE,"E10");Q6=makeQuery(id+"F0.imprint","IMPRINT",FACE,{"disambiguationData":[TD([[makeQuery(id+"F0.imprint","IMPRINT",EDGE,{"derivedFrom":subQ0}),1.0]])]});}
            var Q7;
            {var subQ0=sQuery(id+"F0.wireOp",EDGE,"E15");var subQ5=sQuery(id+"F0.wireOp",EDGE,"E11");var subQ6=makeQuery(id+"F0.imprint","INTERSECT",VERTEX,{"derivedFrom":[subQ5,subQ0]});Q7=makeQuery(id+"F0.imprint","IMPRINT",FACE,{"disambiguationData":[TD([[makeQuery(id+"F0.imprint","IMPRINT",EDGE,{"disambiguationData":[TD([[subQ6,-1.0]])],"derivedFrom":subQ5}),1.0]])]});}
            var Q8;
            {var subQ0=sQuery(id+"F0.wireOp",EDGE,"E9");Q8=makeQuery(id+"F0.imprint","IMPRINT",FACE,{"disambiguationData":[TD([[makeQuery(id+"F0.imprint","IMPRINT",EDGE,{"derivedFrom":subQ0}),1.0]])]});}
            var Q9;
            {var subQ2=sQuery(id+"F0.wireOp",EDGE,"E10");Q9=makeQuery(id+"F0.imprint","IMPRINT",FACE,{"disambiguationData":[TD([[makeQuery(id+"F0.imprint","IMPRINT",EDGE,{"derivedFrom":subQ2}),-1.0]])]});}
            var Q10;
            {var subQ5=sQuery(id+"F0.wireOp",EDGE,"E19");Q10=makeQuery(id+"F0.imprint","IMPRINT",FACE,{"disambiguationData":[TD([[makeQuery(id+"F0.imprint","IMPRINT",EDGE,{"derivedFrom":subQ5}),1.0]])]});}
            var Q11;
            {var subQ0=sQuery(id+"F0.wireOp",EDGE,"E18");var subQ5=sQuery(id+"F0.wireOp",EDGE,"E11");var subQ6=makeQuery(id+"F0.imprint","INTERSECT",VERTEX,{"derivedFrom":[subQ5,subQ0]});Q11=makeQuery(id+"F0.imprint","IMPRINT",FACE,{"disambiguationData":[TD([[makeQuery(id+"F0.imprint","IMPRINT",EDGE,{"disambiguationData":[TD([[subQ6,-1.0]])],"derivedFrom":subQ5}),1.0]])]});}
            var Q12;
            {var subQ0=sQuery(id+"F0.wireOp",EDGE,"E11");var subQ1=sQuery(id+"F0.wireOp",EDGE,"E7");var subQ2=makeQuery(id+"F0.imprint","INTERSECT",VERTEX,{"derivedFrom":[subQ1,subQ0]});Q12=makeQuery(id+"F0.imprint","IMPRINT",FACE,{"disambiguationData":[TD([[makeQuery(id+"F0.imprint","IMPRINT",EDGE,{"disambiguationData":[TD([[subQ2,1.0]])],"derivedFrom":subQ0}),1.0]])]});}
            var Q13;
            {var subQ4=sQuery(id+"F0.wireOp",EDGE,"E9");Q13=makeQuery(id+"F0.imprint","IMPRINT",FACE,{"disambiguationData":[TD([[makeQuery(id+"F0.imprint","IMPRINT",EDGE,{"derivedFrom":subQ4}),-1.0]])]});}
            var Q14;
            {var subQ0=sQuery(id+"F0.wireOp",EDGE,"E14");var subQ5=sQuery(id+"F0.wireOp",EDGE,"E24");var subQ6=makeQuery(id+"F0.imprint","INTERSECT",VERTEX,{"derivedFrom":[subQ0,subQ5]});Q14=makeQuery(id+"F0.imprint","IMPRINT",FACE,{"disambiguationData":[TD([[makeQuery(id+"F0.imprint","IMPRINT",EDGE,{"disambiguationData":[TD([[subQ6,1.0]])],"derivedFrom":subQ5}),1.0]])]});}
            var Q15;
            {var subQ0=sQuery(id+"F0.wireOp",EDGE,"E13");var subQ1=sQuery(id+"F0.wireOp",EDGE,"E4");var subQ2=makeQuery(id+"F0.imprint","INTERSECT",VERTEX,{"derivedFrom":[subQ1,subQ0]});Q15=makeQuery(id+"F0.imprint","IMPRINT",FACE,{"disambiguationData":[TD([[makeQuery(id+"F0.imprint","IMPRINT",EDGE,{"disambiguationData":[TD([[subQ2,-1.0]])],"derivedFrom":subQ1}),1.0]])]});}
            var Q16;
            {var subQ0=sQuery(id+"F0.wireOp",EDGE,"E13");var subQ1=sQuery(id+"F0.wireOp",EDGE,"E4");var subQ2=makeQuery(id+"F0.imprint","INTERSECT",VERTEX,{"derivedFrom":[subQ1,subQ0]});Q16=makeQuery(id+"F0.imprint","IMPRINT",FACE,{"disambiguationData":[TD([[makeQuery(id+"F0.imprint","IMPRINT",EDGE,{"disambiguationData":[TD([[subQ2,-1.0]])],"derivedFrom":subQ1}),-1.0]])]});}
            var Q17;
            {var subQ0=sQuery(id+"F0.wireOp",EDGE,"E24");var subQ4=sQuery(id+"F0.wireOp",EDGE,"E6");var subQ6=makeQuery(id+"F0.imprint","INTERSECT",VERTEX,{"derivedFrom":[subQ4,subQ0]});Q17=makeQuery(id+"F0.imprint","IMPRINT",FACE,{"disambiguationData":[TD([[makeQuery(id+"F0.imprint","IMPRINT",EDGE,{"disambiguationData":[TD([[subQ6,-1.0]])],"derivedFrom":subQ4}),1.0]])]});}
            var Q18;
            {var subQ0=sQuery(id+"F0.wireOp",EDGE,"E8");var subQ1=sQuery(id+"F0.wireOp",EDGE,"E6");var subQ2=makeQuery(id+"F0.imprint","INTERSECT",VERTEX,{"disambiguationData":[OD(0.0)],"derivedFrom":[subQ1,subQ0]});Q18=makeQuery(id+"F0.imprint","IMPRINT",FACE,{"disambiguationData":[TD([[makeQuery(id+"F0.imprint","IMPRINT",EDGE,{"disambiguationData":[TD([[subQ2,-1.0]])],"derivedFrom":subQ1}),1.0]])]});}
            var Q19;
            {var subQ0=sQuery(id+"F0.wireOp",EDGE,"E24");var subQ1=sQuery(id+"F0.wireOp",EDGE,"E2");var subQ2=makeQuery(id+"F0.imprint","INTERSECT",VERTEX,{"derivedFrom":[subQ1,subQ0]});Q19=makeQuery(id+"F0.imprint","IMPRINT",FACE,{"disambiguationData":[TD([[makeQuery(id+"F0.imprint","IMPRINT",EDGE,{"disambiguationData":[TD([[subQ2,-1.0]])],"derivedFrom":subQ0}),1.0]])]});}
            var Q20;
            {var subQ0=sQuery(id+"F0.wireOp",EDGE,"E24");var subQ3=sQuery(id+"F0.wireOp",EDGE,"E7");var subQ5=makeQuery(id+"F0.imprint","INTERSECT",VERTEX,{"derivedFrom":[subQ3,subQ0]});Q20=makeQuery(id+"F0.imprint","IMPRINT",FACE,{"disambiguationData":[TD([[makeQuery(id+"F0.imprint","IMPRINT",EDGE,{"disambiguationData":[TD([[subQ5,-1.0]])],"derivedFrom":subQ0}),1.0]])]});}
            var Q21;
            {var subQ6=sQuery(id+"F0.wireOp",EDGE,"E25");Q21=makeQuery(id+"F0.imprint","IMPRINT",FACE,{"disambiguationData":[TD([[makeQuery(id+"F0.imprint","IMPRINT",EDGE,{"derivedFrom":subQ6}),-1.0]])]});}
            var Q22;
            {var subQ0=sQuery(id+"F0.wireOp",EDGE,"E11");var subQ1=sQuery(id+"F0.wireOp",EDGE,"E2");var subQ2=makeQuery(id+"F0.imprint","INTERSECT",VERTEX,{"derivedFrom":[subQ1,subQ0]});Q22=makeQuery(id+"F0.imprint","IMPRINT",FACE,{"disambiguationData":[TD([[makeQuery(id+"F0.imprint","IMPRINT",EDGE,{"disambiguationData":[TD([[subQ2,-1.0]])],"derivedFrom":subQ0}),1.0]])]});}
            var Q23;
            {var subQ0=sQuery(id+"F0.wireOp",EDGE,"E11");var subQ3=sQuery(id+"F0.wireOp",EDGE,"E7");var subQ5=makeQuery(id+"F0.imprint","INTERSECT",VERTEX,{"derivedFrom":[subQ3,subQ0]});Q23=makeQuery(id+"F0.imprint","IMPRINT",FACE,{"disambiguationData":[TD([[makeQuery(id+"F0.imprint","IMPRINT",EDGE,{"disambiguationData":[TD([[subQ5,-1.0]])],"derivedFrom":subQ0}),1.0]])]});}
            var Q24;
            {var subQ3=sQuery(id+"F0.wireOp",EDGE,"E8");var subQ4=sQuery(id+"F0.wireOp",EDGE,"E6");var subQ6=makeQuery(id+"F0.imprint","INTERSECT",VERTEX,{"disambiguationData":[OD(1.0)],"derivedFrom":[subQ4,subQ3]});Q24=makeQuery(id+"F0.imprint","IMPRINT",FACE,{"disambiguationData":[TD([[makeQuery(id+"F0.imprint","IMPRINT",EDGE,{"disambiguationData":[TD([[subQ6,-1.0]])],"derivedFrom":subQ4}),-1.0]])]});}
            var Q25;
            {var subQ0=sQuery(id+"F0.wireOp",EDGE,"E8");var subQ1=sQuery(id+"F0.wireOp",EDGE,"E6");var subQ2=makeQuery(id+"F0.imprint","INTERSECT",VERTEX,{"disambiguationData":[OD(1.0)],"derivedFrom":[subQ1,subQ0]});Q25=makeQuery(id+"F0.imprint","IMPRINT",FACE,{"disambiguationData":[TD([[makeQuery(id+"F0.imprint","IMPRINT",EDGE,{"disambiguationData":[TD([[subQ2,1.0]])],"derivedFrom":subQ1}),-1.0]])]});}
            var Q26;
            {var subQ3=sQuery(id+"F0.wireOp",EDGE,"E6");var subQ5=sQuery(id+"F0.wireOp",EDGE,"E8");var subQ6=makeQuery(id+"F0.imprint","INTERSECT",VERTEX,{"disambiguationData":[OD(1.0)],"derivedFrom":[subQ3,subQ5]});Q26=makeQuery(id+"F0.imprint","IMPRINT",FACE,{"disambiguationData":[TD([[makeQuery(id+"F0.imprint","IMPRINT",EDGE,{"disambiguationData":[TD([[subQ6,-1.0]])],"derivedFrom":subQ3}),1.0]])]});}
            var Q27;
            {var subQ0=sQuery(id+"F0.wireOp",EDGE,"E30");var subQ1=sQuery(id+"F0.wireOp",EDGE,"E5");var subQ2=makeQuery(id+"F0.imprint","INTERSECT",VERTEX,{"derivedFrom":[subQ1,subQ0]});Q27=makeQuery(id+"F0.imprint","IMPRINT",FACE,{"disambiguationData":[TD([[makeQuery(id+"F0.imprint","IMPRINT",EDGE,{"disambiguationData":[TD([[subQ2,-1.0]])],"derivedFrom":subQ1}),-1.0]])]});}
            var Q28;
            {var subQ1=sQuery(id+"F0.wireOp",EDGE,"E3");var subQ7=sQuery(id+"F0.wireOp",EDGE,"E29");var subQ9=makeQuery(id+"F0.imprint","INTERSECT",VERTEX,{"derivedFrom":[subQ1,subQ7]});Q28=makeQuery(id+"F0.imprint","IMPRINT",FACE,{"disambiguationData":[TD([[makeQuery(id+"F0.imprint","IMPRINT",EDGE,{"disambiguationData":[TD([[subQ9,-1.0]])],"derivedFrom":subQ1}),-1.0]])]});}
            var Q29;
            {var subQ0=sQuery(id+"F0.wireOp",EDGE,"E29");var subQ1=sQuery(id+"F0.wireOp",EDGE,"E3");var subQ2=makeQuery(id+"F0.imprint","INTERSECT",VERTEX,{"derivedFrom":[subQ1,subQ0]});Q29=makeQuery(id+"F0.imprint","IMPRINT",FACE,{"disambiguationData":[TD([[makeQuery(id+"F0.imprint","IMPRINT",EDGE,{"disambiguationData":[TD([[subQ2,-1.0]])],"derivedFrom":subQ1}),1.0]])]});}
            extrude(context, id + "F3", {"entities" : qUnion([Q0, Q1, Q2, Q3, Q4, Q5, Q6, Q7, Q8, Q9, Q10, Q11, Q12, Q13, Q14, Q15, Q16, Q17, Q18, Q19, Q20, Q21, Q22, Q23, Q24, Q25, Q26, Q27, Q28, Q29]), "operationType" : NewBodyOperationType.ADD, "depth" : 6.6 * mm, "hasSecondDirection" : true, "secondDirectionOppositeDirection" : true, "secondDirectionDepth" : 6.6 * mm});
        }
        {
            var Q0;
            Q0=qCreatedBy(makeId("Top.planeOp"),FACE);
            cPlane(context, id + "F4", {"entities" : qUnion([Q0]), "cplaneType" : CPlaneType.OFFSET, "offset" : 53.34 * mm, "oppositeDirection" : true, "width" : 152.4 * mm, "height" : 152.4 * mm});
        }
        {
            var Q0;
            Q0=qCreatedBy(id+"F4.planeOp",FACE);
            var sketch = newSketch(context, id + "F5", { "sketchPlane" : qUnion([Q0])});
            skEllipse(sketch, "E31", {"center": v(0, -1.35) * mm, "majorRadius": 76.2 * mm, "minorRadius": 37.53 * mm, "majorAxis": v(1, 0)});
            skSolve(sketch);
        }
        {
            var Q0;
            Q0 = qSketchRegion(id + "F5", true);
            extrude(context, id + "F6", {"entities" : qUnion([Q0]), "operationType" : NewBodyOperationType.ADD, "oppositeDirection" : true, "depth" : 6.35 * mm});
        }
        {
            var Q0;
            {var subQ0=sQuery(id+"F0.wireOp",EDGE,"E11");var subQ2=makeQuery(id+"F0.imprint","INTERSECT",VERTEX,{"derivedFrom":[sQuery(id+"F0.wireOp",EDGE,"E3"),subQ0]});var subQ3=makeQuery(id+"F0.imprint","INTERSECT",VERTEX,{"derivedFrom":[sQuery(id+"F0.wireOp",EDGE,"E2"),subQ0]});var subQ4=makeQuery(id+"F0.imprint","INTERSECT",VERTEX,{"derivedFrom":[sQuery(id+"F0.wireOp",EDGE,"E7"),subQ0]});Q0=makeQuery(id+"F3.opExtrude","CAP_EDGE",EDGE,{"disambiguationData":[OSD([subQ0]),TDD([makeQuery(id+"F0.imprint","IMPRINT",EDGE,{"disambiguationData":[TD([[subQ4,1.0]])],"derivedFrom":subQ0}),makeQuery(id+"F0.imprint","IMPRINT",EDGE,{"disambiguationData":[TD([[subQ4,-1.0]])],"derivedFrom":subQ0}),makeQuery(id+"F0.imprint","IMPRINT",EDGE,{"disambiguationData":[TD([[subQ3,-1.0]])],"derivedFrom":subQ0}),makeQuery(id+"F0.imprint","IMPRINT",EDGE,{"disambiguationData":[TD([[subQ2,-1.0]])],"derivedFrom":subQ0}),makeQuery(id+"F0.imprint","IMPRINT",EDGE,{"disambiguationData":[TD([[makeQuery(id+"F0.imprint","INTERSECT",VERTEX,{"derivedFrom":[subQ0,sQuery(id+"F0.wireOp",EDGE,"E28")]}),1.0]])],"derivedFrom":subQ0})])],"isStart":false});}
            var Q1;
            {var subQ0=sQuery(id+"F0.wireOp",EDGE,"E24");var subQ1=makeQuery(id+"F0.imprint","INTERSECT",VERTEX,{"derivedFrom":[sQuery(id+"F0.wireOp",EDGE,"E6"),subQ0]});var subQ2=makeQuery(id+"F0.imprint","INTERSECT",VERTEX,{"derivedFrom":[sQuery(id+"F0.wireOp",EDGE,"E3"),subQ0]});var subQ3=makeQuery(id+"F0.imprint","INTERSECT",VERTEX,{"derivedFrom":[sQuery(id+"F0.wireOp",EDGE,"E2"),subQ0]});var subQ4=makeQuery(id+"F0.imprint","INTERSECT",VERTEX,{"derivedFrom":[sQuery(id+"F0.wireOp",EDGE,"E7"),subQ0]});Q1=makeQuery(id+"F3.opExtrude","CAP_EDGE",EDGE,{"disambiguationData":[OSD([subQ0]),TDD([makeQuery(id+"F0.imprint","IMPRINT",EDGE,{"disambiguationData":[TD([[makeQuery(id+"F0.imprint","INTERSECT",VERTEX,{"derivedFrom":[subQ0,sQuery(id+"F0.wireOp",EDGE,"E25")]}),-1.0]])],"derivedFrom":subQ0}),makeQuery(id+"F0.imprint","IMPRINT",EDGE,{"disambiguationData":[TD([[subQ4,-1.0]])],"derivedFrom":subQ0}),makeQuery(id+"F0.imprint","IMPRINT",EDGE,{"disambiguationData":[TD([[subQ3,-1.0]])],"derivedFrom":subQ0}),makeQuery(id+"F0.imprint","IMPRINT",EDGE,{"disambiguationData":[TD([[subQ2,-1.0]])],"derivedFrom":subQ0}),makeQuery(id+"F0.imprint","IMPRINT",EDGE,{"disambiguationData":[TD([[subQ1,-1.0]])],"derivedFrom":subQ0})])],"isStart":false});}
            var Q2;
            {var subQ0=sQuery(id+"F0.wireOp",EDGE,"E11");var subQ2=makeQuery(id+"F0.imprint","INTERSECT",VERTEX,{"derivedFrom":[sQuery(id+"F0.wireOp",EDGE,"E3"),subQ0]});var subQ3=makeQuery(id+"F0.imprint","INTERSECT",VERTEX,{"derivedFrom":[sQuery(id+"F0.wireOp",EDGE,"E2"),subQ0]});var subQ4=makeQuery(id+"F0.imprint","INTERSECT",VERTEX,{"derivedFrom":[sQuery(id+"F0.wireOp",EDGE,"E7"),subQ0]});Q2=makeQuery(id+"F3.opExtrude","CAP_EDGE",EDGE,{"disambiguationData":[OSD([subQ0]),TDD([makeQuery(id+"F0.imprint","IMPRINT",EDGE,{"disambiguationData":[TD([[subQ4,1.0]])],"derivedFrom":subQ0}),makeQuery(id+"F0.imprint","IMPRINT",EDGE,{"disambiguationData":[TD([[subQ4,-1.0]])],"derivedFrom":subQ0}),makeQuery(id+"F0.imprint","IMPRINT",EDGE,{"disambiguationData":[TD([[subQ3,-1.0]])],"derivedFrom":subQ0}),makeQuery(id+"F0.imprint","IMPRINT",EDGE,{"disambiguationData":[TD([[subQ2,-1.0]])],"derivedFrom":subQ0}),makeQuery(id+"F0.imprint","IMPRINT",EDGE,{"disambiguationData":[TD([[makeQuery(id+"F0.imprint","INTERSECT",VERTEX,{"derivedFrom":[subQ0,sQuery(id+"F0.wireOp",EDGE,"E28")]}),1.0]])],"derivedFrom":subQ0})])],"isStart":true});}
            var Q3;
            {var subQ0=sQuery(id+"F0.wireOp",EDGE,"E24");var subQ1=makeQuery(id+"F0.imprint","INTERSECT",VERTEX,{"derivedFrom":[sQuery(id+"F0.wireOp",EDGE,"E6"),subQ0]});var subQ2=makeQuery(id+"F0.imprint","INTERSECT",VERTEX,{"derivedFrom":[sQuery(id+"F0.wireOp",EDGE,"E3"),subQ0]});var subQ3=makeQuery(id+"F0.imprint","INTERSECT",VERTEX,{"derivedFrom":[sQuery(id+"F0.wireOp",EDGE,"E2"),subQ0]});var subQ4=makeQuery(id+"F0.imprint","INTERSECT",VERTEX,{"derivedFrom":[sQuery(id+"F0.wireOp",EDGE,"E7"),subQ0]});Q3=makeQuery(id+"F3.opExtrude","CAP_EDGE",EDGE,{"disambiguationData":[OSD([subQ0]),TDD([makeQuery(id+"F0.imprint","IMPRINT",EDGE,{"disambiguationData":[TD([[makeQuery(id+"F0.imprint","INTERSECT",VERTEX,{"derivedFrom":[subQ0,sQuery(id+"F0.wireOp",EDGE,"E25")]}),-1.0]])],"derivedFrom":subQ0}),makeQuery(id+"F0.imprint","IMPRINT",EDGE,{"disambiguationData":[TD([[subQ4,-1.0]])],"derivedFrom":subQ0}),makeQuery(id+"F0.imprint","IMPRINT",EDGE,{"disambiguationData":[TD([[subQ3,-1.0]])],"derivedFrom":subQ0}),makeQuery(id+"F0.imprint","IMPRINT",EDGE,{"disambiguationData":[TD([[subQ2,-1.0]])],"derivedFrom":subQ0}),makeQuery(id+"F0.imprint","IMPRINT",EDGE,{"disambiguationData":[TD([[subQ1,-1.0]])],"derivedFrom":subQ0})])],"isStart":true});}
            fillet(context, id + "F7", {"entities" : qUnion([Q0, Q1, Q2, Q3]), "radius" : 1.27 * mm, "tangentPropagation" : true, "rho" : .5, "crossSection" : FilletCrossSection.CONIC, "allowEdgeOverflow" : false});
        }
    });
